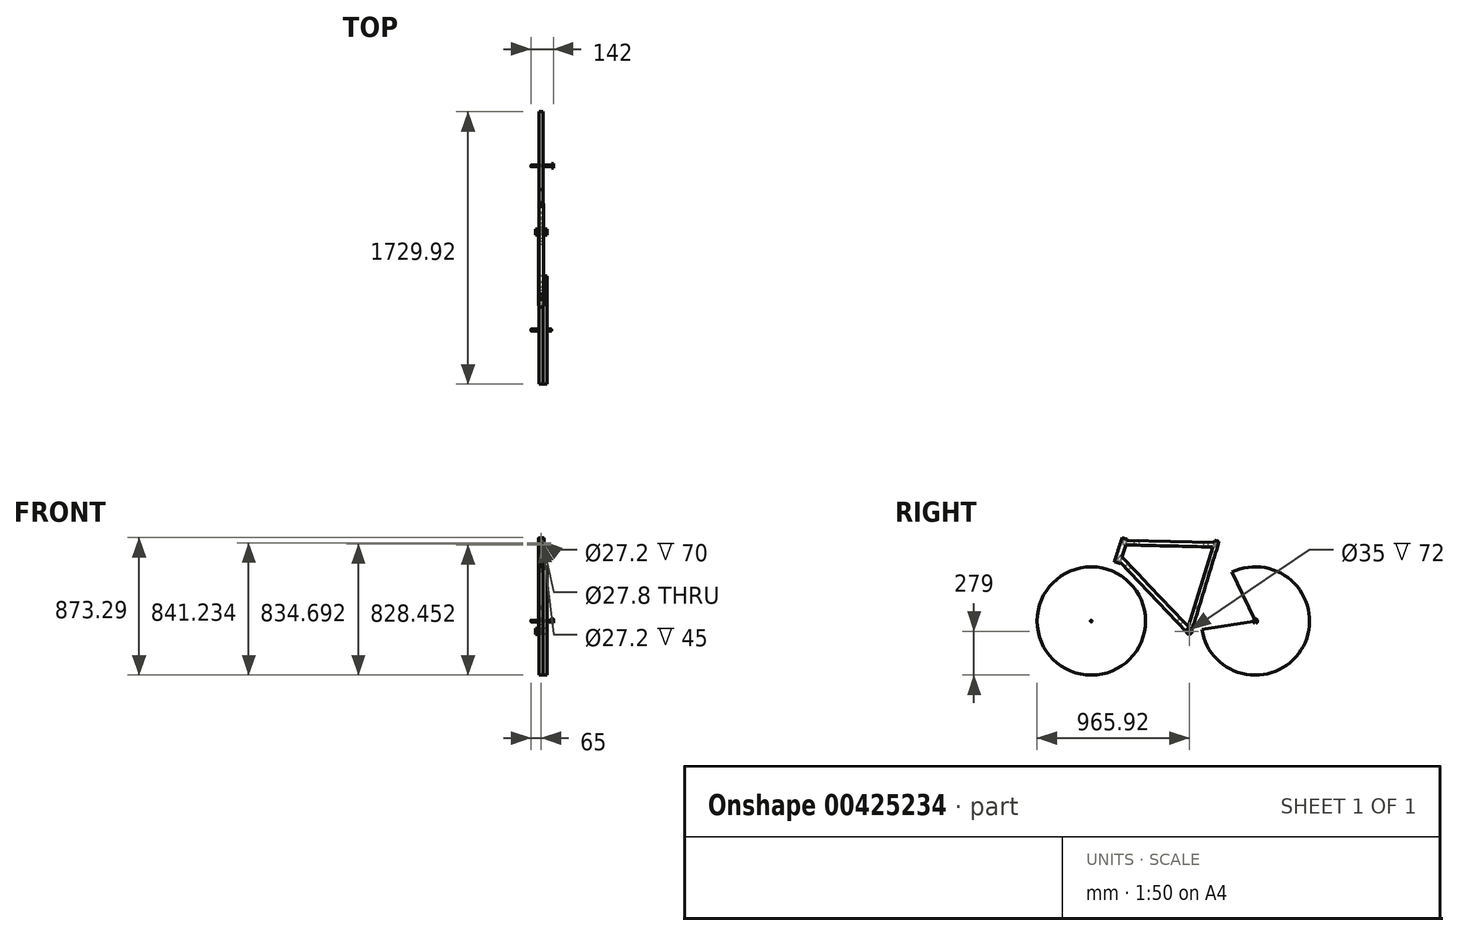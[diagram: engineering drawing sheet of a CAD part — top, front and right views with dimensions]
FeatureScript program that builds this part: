
annotation { "Feature Type Name" : "Feature", "Feature Type Description" : "" }
export const myFeature = defineFeature(function(context is Context, id is Id, definition is map)
    precondition{}
    {
        {
            var Q0;
            Q0=qCreatedBy(makeId("Right.planeOp"),FACE);
            var sketch = newSketch(context, id + "F0", { "sketchPlane" : qUnion([Q0])});
            skLineSegment(sketch, "E0", {"start": v(175.42, 508.78) * mm, "end": v(-409.58, 523.82) * mm});
            skLineSegment(sketch, "E1", {"start": v(-409.58, 523.82) * mm, "end": v(-457.69, 371.22) * mm});
            skLineSegment(sketch, "E2", {"start": v(175.42, 508.78) * mm, "end": v(0, -65) * mm});
            skLineSegment(sketch, "E3", {"start": v(0, -65) * mm, "end": v(420, 0) * mm});
            skLineSegment(sketch, "E4", {"start": v(175.42, 508.78) * mm, "end": v(420, 0) * mm});
            skLineSegment(sketch, "E5", {"start": v(-457.69, 371.22) * mm, "end": v(0, -65) * mm});
            skLineSegment(sketch, "E6", {"start": v(-409.58, 523.82) * mm, "end": v(-574.74, 0) * mm, "construction": true});
            skLineSegment(sketch, "E7", {"start": v(-456.76, 523.82) * mm, "end": v(-621.92, 0) * mm, "construction": true});
            skLineSegment(sketch, "E8", {"start": v(-621.92, 0) * mm, "end": v(420, 0) * mm, "construction": true});
            skLineSegment(sketch, "E9", {"start": v(-457.69, 371.22) * mm, "end": v(-461, 360.73) * mm});
            skLineSegment(sketch, "E10", {"start": v(-461, 360.73) * mm, "end": v(-621.92, 0) * mm});
            skLineSegment(sketch, "E11", {"start": v(-409.58, 523.82) * mm, "end": v(-391.53, 581.04) * mm});
            skLineSegment(sketch, "E12", {"start": v(-391.53, 581.04) * mm, "end": v(-654.6, 663.98) * mm, "construction": true});
            skLineSegment(sketch, "E13", {"start": v(-391.53, 581.04) * mm, "end": v(-514.03, 605.96) * mm});
            skCircle(sketch, "E14", {"center": v(-621.92, 0) * mm, "radius": 344 * mm});
            skCircle(sketch, "E15", {"center": v(420, 0) * mm, "radius": 344 * mm});
            skSolve(sketch);
        }
        {
            var Q0;
            Q0=qCreatedBy(makeId("Right.planeOp"),FACE);
            var sketch = newSketch(context, id + "F1", { "sketchPlane" : qUnion([Q0])});
            skLineSegment(sketch, "E16", {"start": v(-426.93, 529.3) * mm, "end": v(-475.05, 376.7) * mm});
            skLineSegment(sketch, "E17", {"start": v(-387.73, 593.1) * mm, "end": v(-482.6, 292.23) * mm, "construction": true});
            skLineSegment(sketch, "E18", {"start": v(-434.15, 628.31) * mm, "end": v(-424.68, 628.31) * mm});
            skLineSegment(sketch, "E19", {"start": v(-409.58, 523.82) * mm, "end": v(-426.93, 529.3) * mm, "construction": true});
            skLineSegment(sketch, "E20", {"start": v(-457.69, 371.22) * mm, "end": v(-475.05, 376.7) * mm, "construction": true});
            skLineSegment(sketch, "E21", {"start": v(-426.93, 529.3) * mm, "end": v(-425.8, 528.93) * mm});
            skLineSegment(sketch, "E22", {"start": v(-425.8, 528.93) * mm, "end": v(-473.9, 376.34) * mm});
            skLineSegment(sketch, "E23", {"start": v(-473.9, 376.34) * mm, "end": v(-475.05, 376.7) * mm});
            skSolve(sketch);
        }
        {
            var Q0;
            Q0=makeQuery(id+"F1.imprint","IMPRINT",FACE,{"disambiguationData":[TD([[makeQuery(id+"F1.imprint","IMPRINT",EDGE,{"derivedFrom":sQuery(id+"F1.wireOp",EDGE,"E16")}),1.0]])]});
            var Q1;
            Q1=sQuery(id+"F1.wireOp",EDGE,"E17");
            revolve(context, id + "F2", {"entities" : qUnion([Q0]), "axis" : qUnion([Q1]), "revolveType" : RevolveType.FULL});
        }
        {
            var Q0;
            Q0=qCreatedBy(makeId("Right.planeOp"),FACE);
            var sketch = newSketch(context, id + "F3", { "sketchPlane" : qUnion([Q0])});
            skCircle(sketch, "E24", {"center": v(0, -65) * mm, "radius": 17.5 * mm});
            skSolve(sketch);
        }
        {
            var Q0;
            Q0=makeQuery(id+"F3.imprint","IMPRINT",FACE,{"disambiguationData":[TD([[makeQuery(id+"F3.imprint","IMPRINT",EDGE,{"derivedFrom":sQuery(id+"F3.wireOp",EDGE,"E24")}),1.0]])]});
            var Q1;
            Q1=sQuery(id+"F3.wireOp",EDGE,"E24");
            extrude(context, id + "F4", {"entities" : qUnion([Q0]), "surfaceEntities" : qUnion([Q1]), "endBound" : BoundingType.SYMMETRIC, "depth" : 72 * mm});
        }
        {
            var Q0;
            Q0=makeQuery(id+"F4.opExtrude","CAP_FACE",FACE,{"disambiguationData":[OSD([sQuery(id+"F3.wireOp",EDGE,"E24")])],"isStart":false});
            var Q1;
            Q1=makeQuery(id+"F4.opExtrude","CAP_FACE",FACE,{"disambiguationData":[OSD([sQuery(id+"F3.wireOp",EDGE,"E24")])],"isStart":true});
            shell(context, id + "F5", {"entities" : qUnion([Q0, Q1]), "thickness" : 1.5 * mm, "oppositeDirection" : true});
        }
        {
            var Q0;
            Q0=qCreatedBy(makeId("Right.planeOp"),FACE);
            var sketch = newSketch(context, id + "F6", { "sketchPlane" : qUnion([Q0])});
            skLineSegment(sketch, "E25", {"start": v(-27.84, -156.08) * mm, "end": v(195.05, 572.96) * mm, "construction": true});
            skLineSegment(sketch, "E26", {"start": v(175.42, 508.78) * mm, "end": v(161.75, 512.96) * mm, "construction": true});
            skLineSegment(sketch, "E27", {"start": v(0, -65) * mm, "end": v(-47.6, -50.45) * mm, "construction": true});
            skLineSegment(sketch, "E28", {"start": v(161.75, 512.96) * mm, "end": v(-13.68, -60.82) * mm});
            skPoint(sketch, "E28.endSnap0", {"position": v(-13.68, -60.82) * mm});
            skLineSegment(sketch, "E29", {"start": v(161.75, 512.96) * mm, "end": v(162.32, 512.79) * mm});
            skLineSegment(sketch, "E30", {"start": v(162.32, 512.79) * mm, "end": v(115.54, 359.78) * mm});
            skLineSegment(sketch, "E31", {"start": v(115.54, 359.78) * mm, "end": v(106.58, 331.15) * mm});
            skLineSegment(sketch, "E32", {"start": v(106.58, 331.15) * mm, "end": v(33.18, 91.08) * mm});
            skLineSegment(sketch, "E33", {"start": v(33.18, 91.08) * mm, "end": v(33.18, 81.7) * mm});
            skLineSegment(sketch, "E34", {"start": v(33.18, 81.7) * mm, "end": v(-10.67, -61.74) * mm});
            skLineSegment(sketch, "E35", {"start": v(-10.67, -61.74) * mm, "end": v(-13.68, -60.82) * mm});
            skSolve(sketch);
        }
        {
            var Q0;
            Q0=qSketchRegion(id+"F6",true);
            var Q1;
            Q1=sQuery(id+"F6.wireOp",EDGE,"E25");
            revolve(context, id + "F7", {"operationType" : NewBodyOperationType.ADD, "entities" : qUnion([Q0]), "axis" : qUnion([Q1]), "revolveType" : RevolveType.FULL});
        }
        {
            var Q0;
            Q0=qCreatedBy(makeId("Right.planeOp"),FACE);
            var sketch = newSketch(context, id + "F8", { "sketchPlane" : qUnion([Q0])});
            skLineSegment(sketch, "E36", {"start": v(0, -65) * mm, "end": v(-447.17, 404.6) * mm, "construction": true});
            skLineSegment(sketch, "E37", {"start": v(-447.17, 404.6) * mm, "end": v(-435.69, 415.53) * mm, "construction": true});
            skLineSegment(sketch, "E38", {"start": v(-435.69, 415.53) * mm, "end": v(11.48, -54.07) * mm});
            skLineSegment(sketch, "E39", {"start": v(0, -65) * mm, "end": v(11.48, -54.07) * mm});
            skLineSegment(sketch, "E40", {"start": v(-435.69, 415.53) * mm, "end": v(-436.2, 415.05) * mm});
            skLineSegment(sketch, "E41", {"start": v(-436.2, 415.05) * mm, "end": v(-387.92, 364.36) * mm});
            skLineSegment(sketch, "E42", {"start": v(-387.92, 364.36) * mm, "end": v(-367.02, 342.84) * mm});
            skLineSegment(sketch, "E43", {"start": v(-367.02, 342.84) * mm, "end": v(-57.77, 18.07) * mm});
            skLineSegment(sketch, "E44", {"start": v(-57.77, 18.07) * mm, "end": v(-37.3, -3.86) * mm});
            skLineSegment(sketch, "E45", {"start": v(-37.3, -3.86) * mm, "end": v(10.97, -54.55) * mm});
            skSolve(sketch);
        }
        {
            var Q0;
            Q0=qSketchRegion(id+"F8",true);
            var Q1;
            Q1=sQuery(id+"F8.wireOp",EDGE,"E36");
            revolve(context, id + "F9", {"entities" : qUnion([Q0]), "axis" : qUnion([Q1]), "revolveType" : RevolveType.FULL});
        }
        {
            var Q0;
            Q0=qCreatedBy(makeId("Right.planeOp"),FACE);
            var sketch = newSketch(context, id + "F10", { "sketchPlane" : qUnion([Q0])});
            skLineSegment(sketch, "E46", {"start": v(-417.7, 498.07) * mm, "end": v(167.82, 483.92) * mm, "construction": true});
            skLineSegment(sketch, "E47", {"start": v(-417.7, 498.07) * mm, "end": v(-417.35, 512.36) * mm});
            skLineSegment(sketch, "E48", {"start": v(-417.35, 512.36) * mm, "end": v(168.17, 498.21) * mm});
            skLineSegment(sketch, "E49", {"start": v(167.82, 483.92) * mm, "end": v(168.17, 498.21) * mm});
            skLineSegment(sketch, "E50", {"start": v(-417.37, 511.67) * mm, "end": v(-347.39, 509.97) * mm});
            skLineSegment(sketch, "E51", {"start": v(-347.39, 509.97) * mm, "end": v(-317.4, 509.55) * mm});
            skLineSegment(sketch, "E52", {"start": v(-317.4, 509.55) * mm, "end": v(93.18, 499.63) * mm});
            skLineSegment(sketch, "E53", {"start": v(93.18, 499.63) * mm, "end": v(123.16, 498.6) * mm});
            skLineSegment(sketch, "E54", {"start": v(123.16, 498.6) * mm, "end": v(168.15, 497.51) * mm});
            skPoint(sketch, "E54.endSnap0", {"position": v(168, 491.07) * mm});
            skSolve(sketch);
        }
        {
            var Q0;
            Q0=qSketchRegion(id+"F10",true);
            var Q1;
            Q1=sQuery(id+"F10.wireOp",EDGE,"E46");
            revolve(context, id + "F11", {"entities" : qUnion([Q0]), "axis" : qUnion([Q1]), "revolveType" : RevolveType.FULL});
        }
        {
            var Q0;
            Q0=sQuery(id+"F0.wireOp",EDGE,"E3");
            cPlane(context, id + "F12", {"entities" : qUnion([Q0]), "cplaneType" : CPlaneType.LINE_ANGLE, "offset" : 150 * mm, "angle" : 0 * degree, "width" : 150 * mm, "height" : 150 * mm});
        }
        {
            var Q0;
            Q0=qCreatedBy(makeId("Right.planeOp"),FACE);
            cPlane(context, id + "F13", {"entities" : qUnion([Q0]), "cplaneType" : CPlaneType.OFFSET, "offset" : 65 * mm, "width" : 150 * mm, "height" : 150 * mm});
        }
        {
            var Q0;
            Q0=qCreatedBy(id+"F13.planeOp",FACE);
            var sketch = newSketch(context, id + "F14", { "sketchPlane" : qUnion([Q0])});
            skArc(sketch, "E55", {"start": v(425, -13.08) * mm, "mid": v(420, 14) * mm, "end": v(415, -13.08) * mm});
            skArc(sketch, "E56", {"start": v(425, 0) * mm, "mid": v(420, 5) * mm, "end": v(415, 0) * mm});
            skLineSegment(sketch, "E57", {"start": v(415, 0) * mm, "end": v(415, -13.08) * mm});
            skLineSegment(sketch, "E58", {"start": v(425, 0) * mm, "end": v(425, -13.08) * mm});
            skSolve(sketch);
        }
        {
            var Q0;
            Q0=qSketchRegion(id+"F14",true);
            extrude(context, id + "F15", {"entities" : qUnion([Q0]), "depth" : 12 * mm});
        }
        {
            var Q0;
            Q0=makeQuery(id+"F15.opExtrude","CAP_FACE",FACE,{"disambiguationData":[OSD([sQuery(id+"F14.wireOp",EDGE,"E55"),sQuery(id+"F14.wireOp",EDGE,"E56"),sQuery(id+"F14.wireOp",EDGE,"E57"),sQuery(id+"F14.wireOp",EDGE,"E58")])],"isStart":false});
            var Q1;
            Q1=makeQuery(id+"F15.opExtrude","SWEPT_FACE",FACE,{"disambiguationData":[OSD([sQuery(id+"F14.wireOp",EDGE,"E57")])]});
            var Q2;
            Q2=makeQuery(id+"F15.opExtrude","SWEPT_FACE",FACE,{"disambiguationData":[OSD([sQuery(id+"F14.wireOp",EDGE,"E56")])]});
            var Q3;
            Q3=makeQuery(id+"F15.opExtrude","SWEPT_FACE",FACE,{"disambiguationData":[OSD([sQuery(id+"F14.wireOp",EDGE,"E58")])]});
            shell(context, id + "F16", {"entities" : qUnion([Q0, Q1, Q2, Q3]), "thickness" : 3 * mm});
        }
        {
            var Q0;
            Q0=qCreatedBy(id+"F12.planeOp",FACE);
            var sketch = newSketch(context, id + "F17", { "sketchPlane" : qUnion([Q0])});
            skLineSegment(sketch, "E59", {"start": v(70, 415.06) * mm, "end": v(30, -9.94) * mm});
            skLineSegment(sketch, "E60", {"start": v(0, 415.06) * mm, "end": v(70, 415.06) * mm, "construction": true});
            skSolve(sketch);
        }
        {
            var Q0;
            Q0=qCreatedBy(makeId("Right.planeOp"),FACE);
            var sketch = newSketch(context, id + "F18", { "sketchPlane" : qUnion([Q0])});
            skCircle(sketch, "E61", {"center": v(-621.92, 0) * mm, "radius": 5 * mm});
            skCircle(sketch, "E62", {"center": v(420, 0) * mm, "radius": 5 * mm});
            skSolve(sketch);
        }
        {
            var Q0;
            Q0=qSketchRegion(id+"F18",true);
            extrude(context, id + "F19", {"entities" : qUnion([Q0]), "endBound" : BoundingType.SYMMETRIC, "depth" : 130 * mm});
        }
        {
            var Q0;
            Q0=makeQuery(id+"F0.imprint","IMPRINT",FACE,{"disambiguationData":[TD([[makeQuery(id+"F0.imprint","IMPRINT",EDGE,{"derivedFrom":sQuery(id+"F0.wireOp",EDGE,"E14")}),1.0]])]});
            var Q1;
            {var subQ0=sQuery(id+"F0.wireOp",EDGE,"E4");var subQ1=sQuery(id+"F0.wireOp",EDGE,"E3");var subQ2=makeQuery(id+"F0.imprint","INTERSECT",VERTEX,{"derivedFrom":[subQ1,subQ0]});Q1=makeQuery(id+"F0.imprint","IMPRINT",FACE,{"disambiguationData":[TD([[makeQuery(id+"F0.imprint","IMPRINT",EDGE,{"disambiguationData":[TD([[subQ2,1.0]])],"derivedFrom":subQ1}),-1.0]])]});}
            extrude(context, id + "F20", {"entities" : qUnion([Q0, Q1]), "endBound" : BoundingType.SYMMETRIC, "depth" : 25 * mm});
        }
        {
            var Q0;
            Q0=sQuery(id+"F0.wireOp",EDGE,"E4");
            extrude(context, id + "F21", {"bodyType" : ToolBodyType.SURFACE, "surfaceEntities" : qUnion([Q0]), "endBound" : BoundingType.SYMMETRIC, "depth" : 25 * mm});
        }
        {
            var Q0;
            Q0=sQuery(id+"F0.wireOp",EDGE,"E3");
            var Q1;
            Q1=sQuery(id+"F17.wireOp",EDGE,"E59");
            extrude(context, id + "F22", {"bodyType" : ToolBodyType.SURFACE, "surfaceEntities" : qUnion([Q0, Q1]), "depth" : 25 * mm});
        }
        {
            var Q0;
            Q0=makeQuery(id+"F20.opExtrude","CAP_FACE",FACE,{"disambiguationData":[OSD([sQuery(id+"F0.wireOp",EDGE,"E14")])],"isStart":false});
            extrude(context, id + "F23", {"entities" : qUnion([Q0]), "depth" : 25 * mm});
        }
        {
            var Q0;
            Q0=makeQuery(id+"F21.opExtrude","SWEPT_BODY",BODY,{"disambiguationData":[OSD([sQuery(id+"F0.wireOp",EDGE,"E4")])]});
            deleteBodies(context, id + "F24", {"entities" : qUnion([Q0])});
        }
        {
            var Q0;
            Q0=makeQuery(id+"F22.opExtrude","SWEPT_BODY",BODY,{"disambiguationData":[OSD([sQuery(id+"F0.wireOp",EDGE,"E3")])]});
            deleteBodies(context, id + "F25", {"entities" : qUnion([Q0])});
        }
        {
            var Q0;
            Q0=makeQuery(id+"F22.opExtrude","SWEPT_BODY",BODY,{"disambiguationData":[OSD([sQuery(id+"F17.wireOp",EDGE,"E59")])]});
            deleteBodies(context, id + "F26", {"entities" : qUnion([Q0])});
        }
    });
